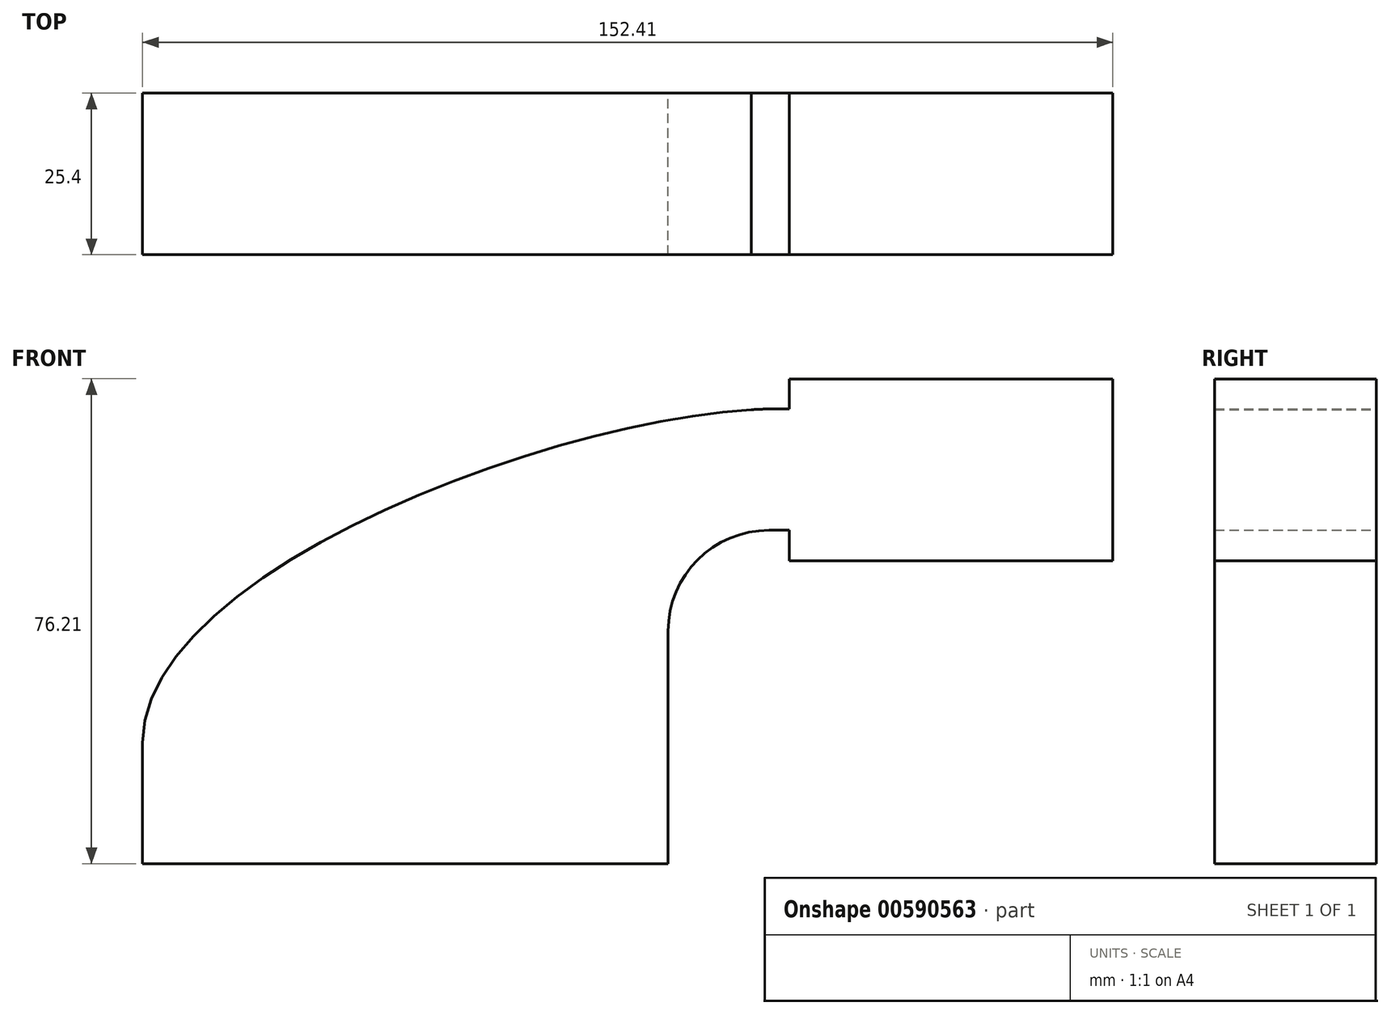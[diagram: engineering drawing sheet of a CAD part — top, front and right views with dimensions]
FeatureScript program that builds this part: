
annotation { "Feature Type Name" : "Feature", "Feature Type Description" : "" }
export const myFeature = defineFeature(function(context is Context, id is Id, definition is map)
    precondition{}
    {
        {
            var Q0;
            Q0=qCreatedBy(makeId("Front.planeOp"),FACE);
            var sketch = newSketch(context, id + "F0", { "sketchPlane" : qUnion([Q0])});
            skLineSegment(sketch, "E0.bottom", {"start": v(-41.28, -9.53) * mm, "end": v(41.28, -9.53) * mm});
            skLineSegment(sketch, "E0.top", {"start": v(-41.28, 9.53) * mm, "end": v(41.28, 9.53) * mm});
            skLineSegment(sketch, "E0.left", {"start": v(-41.28, -9.53) * mm, "end": v(-41.28, 9.53) * mm});
            skLineSegment(sketch, "E0.right", {"start": v(41.28, -9.53) * mm, "end": v(41.28, 9.52) * mm});
            skPoint(sketch, "E0.middle", {"position": v(0, 0) * mm});
            skLineSegment(sketch, "E1.bottom", {"start": v(60.33, 38.1) * mm, "end": v(111.13, 38.1) * mm});
            skLineSegment(sketch, "E1.top", {"start": v(60.33, 66.67) * mm, "end": v(111.13, 66.67) * mm});
            skLineSegment(sketch, "E1.left", {"start": v(60.33, 38.1) * mm, "end": v(60.33, 66.68) * mm});
            skLineSegment(sketch, "E1.right", {"start": v(111.13, 38.1) * mm, "end": v(111.13, 66.68) * mm});
            skPoint(sketch, "E1.middle", {"position": v(85.73, 52.39) * mm});
            skLineSegment(sketch, "E2", {"start": v(41.28, 9.52) * mm, "end": v(41.28, 27) * mm});
            skArc(sketch, "E3", {"start": v(41.27, 27) * mm, "mid": v(45.92, 38.23) * mm, "end": v(57.15, 42.88) * mm});
            skLineSegment(sketch, "E4", {"start": v(57.15, 42.88) * mm, "end": v(78.34, 42.88) * mm});
            skLineSegment(sketch, "E5.0", {"start": v(57.15, 61.93) * mm, "end": v(78.34, 61.93) * mm});
            skArc(sketch, "E5.1", {"start": v(22.23, 27) * mm, "mid": v(32.45, 51.7) * mm, "end": v(57.15, 61.93) * mm});
            skLineSegment(sketch, "E5.2", {"start": v(22.22, 9.52) * mm, "end": v(22.22, 27) * mm});
            skLineSegment(sketch, "E6", {"start": v(78.34, 38.1) * mm, "end": v(78.34, 66.67) * mm});
            skFitSpline(sketch, "E7", {"points": [v(-41.28, 9.53) * mm, v(57.15, 61.93) * mm], "startDerivative": vector(0.36, 81.7) * mm, "endDerivative": vector(96.05, 1.99) * mm});
            skSolve(sketch);
        }
        {
            var Q0;
            Q0 = qSketchRegion(id + "F0", true);
            extrude(context, id + "F1", {"entities" : qUnion([Q0]), "depth" : 25.4 * mm, "offsetDistance" : 25.4 * mm});
        }
    });
